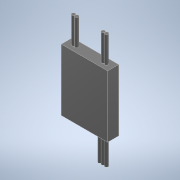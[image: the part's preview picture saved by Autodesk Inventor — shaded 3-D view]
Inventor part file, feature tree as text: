
AUTODESK INVENTOR PART (.ipt)
format: ipt  version: 2022 (Build 260153000, 153)  size: 126,464 bytes
history: native  units: in
note: dims shown in document units (in); Inventor stores cm internally (conversion verified against a paired STEP export)
features: extrude x3, sketch x3
ambient origin geometry x8: Origin, YZ Plane, XZ Plane, XY Plane, X Axis, Y Axis, Z Axis, Center Point
bodies: Solid1 (feature_tree)
feature tree (6):
  extrude  "Extrusion1"  Depth=1.1024in
  extrude  "Extrusion2"  Depth=0.4724in TaperAngle=0.0deg
  extrude  "Extrusion3"  Depth=0.4724in
  sketch  "Sketch1"  dims[d0=0.8268in d1=1.1024in]
  sketch  "Sketch2"  dims[d2=0.1969in d3=0.0in d7=0.4724in d8=0.0in]
  sketch  "Sketch3"  dims[d12=0.4724in d13=0.0in d14=0.0591in d15=0.0591in d16=0.0591in d17=0.1181in d18=0.1181in d19=0.0591in d20=0.0591in d21=0.0591in d22=0.1181in]
